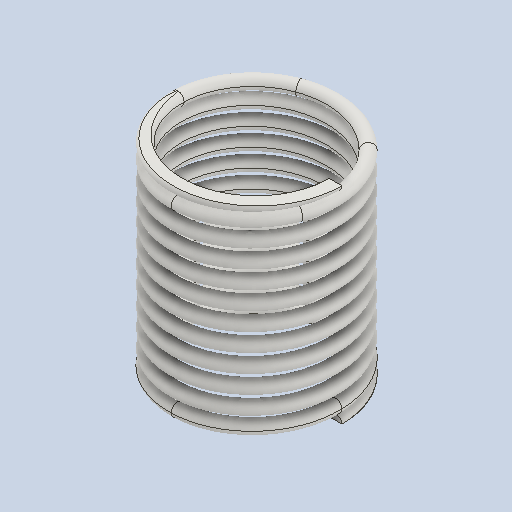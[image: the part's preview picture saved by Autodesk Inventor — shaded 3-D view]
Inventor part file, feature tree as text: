
AUTODESK INVENTOR PART (.ipt)
format: ipt  version: 2025 (Build 290162010, 162A)  size: 1,084,928 bytes
history: native  units: mm
features: other x65, extrude x8, plane x5, helix x3, sketch x3, sweep x2
ambient origin geometry x8: Origin, YZ Plane, XZ Plane, XY Plane, X Axis, Y Axis, Z Axis, Center Point
bodies: Solid1 (feature_tree)
feature tree (86):
  other  "Hauptschraubenpfad(Rechts)"
  other  "Profilarbeitsebene(Rechts)"
  plane  "Arbeitsebene(Rechts) starten"
  plane  "Arbeitsebene(Rechts) beenden"
  other  "Schnittarbeitsebene(Rechts) beenden"
  other  "Schnittarbeitsebene(Rechts) starten"
  other  "Schnittarbeitsebene mit flachen Enden 1(Rechts)"
  other  "Schnittarbeitsebene mit flachen Enden 2(Rechts)"
  sweep  "Main Coil Feature(R)"
  other  "Übergangsschraube 1(Rechts) starten"
  helix  "Coil  Start Transition 2(R)"  [1 undecoded]
  helix  "Coil  Start Transition 3(R)"  [1 undecoded]
  helix  "Coil  Start Transition 4(R)"  [1 undecoded]
  other  "Endenschraube(Rechts) starten"
  extrude  "Schnittelement(Rechts) starten"  Depth=10.0mm
  other  "Übergangsschraube 1(Rechts) beenden"
  other  "Übergangsschraube 2(Rechts) beenden"
  other  "Übergangsschraube 3(Rechts) beenden"
  other  "Übergangsschraube 4(Rechts) beenden"
  other  "Spirale(Rechts) beenden"
  extrude  "Schnittelement(Rechts) beenden"  Depth=10.0mm
  extrude  "Schnittelement mit flachen Enden 1(Rechts)"  Depth=10.0mm
  extrude  "Plain Ends Cut  2(R)"  Depth=10.0mm TaperAngle=0.0deg
  other  "Hauptschraubenpfad(Links)"
  other  "Profilarbeitsebene(Links)"
  plane  "Arbeitsebene(Links) starten"
  plane  "Arbeitsebene(Links) beenden"
  other  "Schnittarbeitsebene(Links) beenden"
  other  "Schnittarbeitsebene(Links) starten"
  other  "Schnittarbeitsebene mit flachen Enden 1(Links)"
  other  "Schnittarbeitsebene mit flachen Enden 2(Links)"
  sweep  "Main Coil Feature(L)"
  other  "Übergangsschraube 1(Links) starten"
  other  "Übergangsschraube 2(Links) starten"
  other  "Übergangsschraube 3(Links) starten"
  other  "Übergangsschraube 4(Links) starten"
  other  "Endenschraube(Links) starten"
  extrude  "Schnittelement(Links) starten"  Depth=10.0mm TaperAngle=0.0deg
  other  "Übergangsschraube 1(Links) beenden"
  other  "Übergangsschraube 2(Links) beenden"
  other  "Übergangsschraube 3(Links) beenden"
  other  "Übergangsschraube 4(Links) beenden"
  other  "Spirale(Links) beenden"
  extrude  "Schnittelement(Links) beenden"  Depth=10.0mm
  extrude  "Cut Plain Ends Cut 1(L)"  TaperAngle=0.0deg  [1 undecoded]
  extrude  "Cut Plain Ends Cut 2(L)"  TaperAngle=0.0deg  [1 undecoded]
  other  "iMate-basierte Arbeitsebene"
  other  "Vorschau Mittelpunkt"
  other  "Vorschau X-Achse"
  other  "Pfadprofilskizze(Rechts)"
  other  "Srf1"
  other  "Spiralenprofilskizze(Rechts)"
  other  "Übergangsschraubenskizze 1(Rechts) starten"
  sketch  "Sketch  Start Transition 2(R)"  dims[d0=0.125mm d2=0.701927mm d3=10.0mm d4=92.5mm]
  sketch  "Sketch  Start Transition 3(R)"  dims[d5=0.0mm d6=90.0deg d7=90.0deg d8=0.0mm d9=0.0mm d12=0.681625mm d13=-0.825556mm d14=0.5mm]
  sketch  "Sketch  Start Transition 4(R)"  dims[d15=0.0mm d16=0.651446mm d17=10.0mm d18=2.5mm d19=0.0mm d20=90.0deg d21=90.0deg d22=0.0mm d23=0.0mm d24=0.600964mm d25=10.0mm d26=2.5mm d27=0.0mm d28=90.0deg d29=90.0deg d30=0.0mm d31=0.0mm d32=0.550482mm d33=10.0mm d34=2.5mm d35=0.0mm d36=90.0deg d37=90.0deg d38=0.0mm d39=0.0mm d40=0.5mm d41=10.0mm d42=2.5mm d43=0.0mm d44=90.0deg d45=90.0deg d46=0.0mm d47=0.0mm d48=0.651446mm d49=10.0mm d50=1.875mm d51=0.0mm d52=90.0deg d53=90.0deg d54=0.0mm d55=0.0mm d56=0.600964mm d57=10.0mm d58=1.875mm d59=0.0mm d60=90.0deg d61=90.0deg d62=0.0mm d63=0.0mm d64=0.550482mm d65=10.0mm d66=1.875mm d67=0.0mm d68=90.0deg d69=90.0deg d70=0.0mm d71=0.0mm d72=0.5mm d73=10.0mm d74=1.875mm d75=0.0mm d76=90.0deg d77=90.0deg d78=0.0mm d79=0.0mm d81=10.0mm d82=5.0mm d83=0.0mm d84=90.0deg d85=90.0deg d86=0.0mm d87=0.0mm d88=0.500334mm d89=10.0mm d90=5.0mm d91=0.0mm d92=90.0deg d93=90.0deg d94=0.0mm d95=0.0mm d96=6.6153mm d97=0.500334mm d98=0.0mm d99=6.6153mm d100=0.500334mm d101=0.0mm d102=0.0mm d103=0.0mm d104=0.0mm d105=0.0mm d106=0.0mm d108=0.0mm d112=0.0mm d113=0.0mm d114=0.0mm d121=0.000334mm d131=0.0mm d132=0.0mm d133=0.0mm d134=0.0mm d135=0.125mm d137=0.701927mm d138=10.0mm d139=92.5mm d140=0.0mm d141=90.0deg d142=90.0deg d143=0.0mm d144=0.0mm d145=0.681625mm d146=-0.825556mm d147=0.000334mm d148=0.000334mm d149=0.5mm d150=0.0mm d151=0.0mm d152=0.651446mm d153=10.0mm d154=2.5mm d155=0.0mm d156=90.0deg d157=90.0deg d158=0.0mm d159=0.0mm d160=0.600964mm d161=10.0mm d162=2.5mm d163=0.0mm d164=90.0deg d165=90.0deg d166=0.0mm d167=0.0mm d168=0.550482mm d169=10.0mm d170=2.5mm d171=0.0mm d172=90.0deg d173=90.0deg d174=0.0mm d175=0.0mm d176=0.5mm d177=10.0mm d178=2.5mm d179=0.0mm d180=90.0deg d181=90.0deg d182=0.0mm d183=0.0mm d184=10.0mm d185=10.0mm d186=10.0mm d187=10.0mm d188=0.500334mm d189=10.0mm d190=5.0mm d191=0.0mm d192=90.0deg d193=90.0deg d194=0.0mm d195=0.0mm d196=10.0mm d197=6.6153mm d198=0.500334mm d199=0.0mm d200=10.0mm d201=0.651446mm d202=10.0mm d203=1.875mm d204=0.0mm d205=90.0deg d206=90.0deg d207=0.0mm d208=0.0mm d209=10.0mm d210=0.600964mm d211=10.0mm d212=1.875mm d213=0.0mm d214=90.0deg d215=90.0deg d216=0.0mm d217=0.0mm d218=0.550482mm d219=10.0mm d220=1.875mm d221=0.0mm d222=90.0deg d223=90.0deg d224=0.0mm d225=0.0mm d226=0.5mm d227=10.0mm d228=1.875mm d229=0.0mm d230=90.0deg d231=90.0deg d232=0.0mm d233=0.0mm d234=10.0mm d235=10.0mm d236=10.0mm d237=0.500334mm d238=10.0mm d239=5.0mm d240=0.0mm d241=90.0deg d242=90.0deg d243=0.0mm d244=0.0mm d245=6.6153mm d246=0.500334mm d247=0.0mm d248=10.0mm d249=10.0mm d254=6.6153mm d255=10.0mm d256=0.0mm d257=20.0mm d258=-0.000334mm d259=6.6153mm d260=10.0mm d261=0.0mm d262=10.0mm d263=6.6153mm d264=10.0mm d265=0.0mm d266=10.0mm d267=0.0mm d270=-0.763056mm d271=0.0mm d272=6.6153mm d273=10.0mm d274=0.0mm d275=20.0mm d276=-94.24778mm d277=6.1153mm d278=6.1153mm d279=0.0mm d280=0.0mm]
  other  "Übergangsschraubenskizze 1(Rechts) beenden"
  other  "Übergangsschraubenskizze 2(Rechts) beenden"
  other  "Übergangsschraubenskizze 3(Rechts) beenden"
  other  "Übergangsschraubenskizze 4(Rechts) beenden"
  other  "Endenskizze(Rechts) starten"
  other  "Spiralenskizze(Rechts) beenden"
  other  "Schnittskizze(Rechts) beenden"
  other  "Schnittskizze (Rechts) starten"
  other  "Pfadprofilskizze(Links)"
  other  "Srf2"
  other  "Spiralenprofilskizze(Links)"
  other  "Übergangsschraubenskizze 1(Links) starten"
  other  "Übergangsschraubenskizze 2(Links) starten"
  other  "Übergangsschraubenskizze 3(Links) starten"
  other  "Übergangsschraubenskizze 4(Links) starten"
  other  "Endenskizze(Links) starten"
  other  "Schnittskizze(Links) starten"
  other  "Übergangsschraubenskizze 1(Links) beenden"
  other  "Übergangsschraubenskizze 2(Links) beenden"
  other  "Übergangsschraubenskizze 3(Links) beenden"
  other  "Übergangsschraubenskizze 4(Links) beenden"
  other  "Spiralenskizze(Links) beenden"
  other  "Schnittskizze(Links) beenden"
  other  "Schnittskizze mit flachen Enden 2(Links)"
  other  "Schnittskizze mit flachen Enden 2(Rechts)"
  other  "Schnittskizze mit flachen Enden 1(Rechts)"
  other  "Schnittskizze mit flachen Enden 1(Links)"
  plane  "Arbeitsebene - Schnitt starten"
  other  "Basiskurve(Rechts)"
  other  "Basiskurve(Links)"
note: 5 required parameter values undecoded (feature->parameter linkage not recoverable at this tier; creation-order binding heuristic only, values carry confidence <= 0.55)
